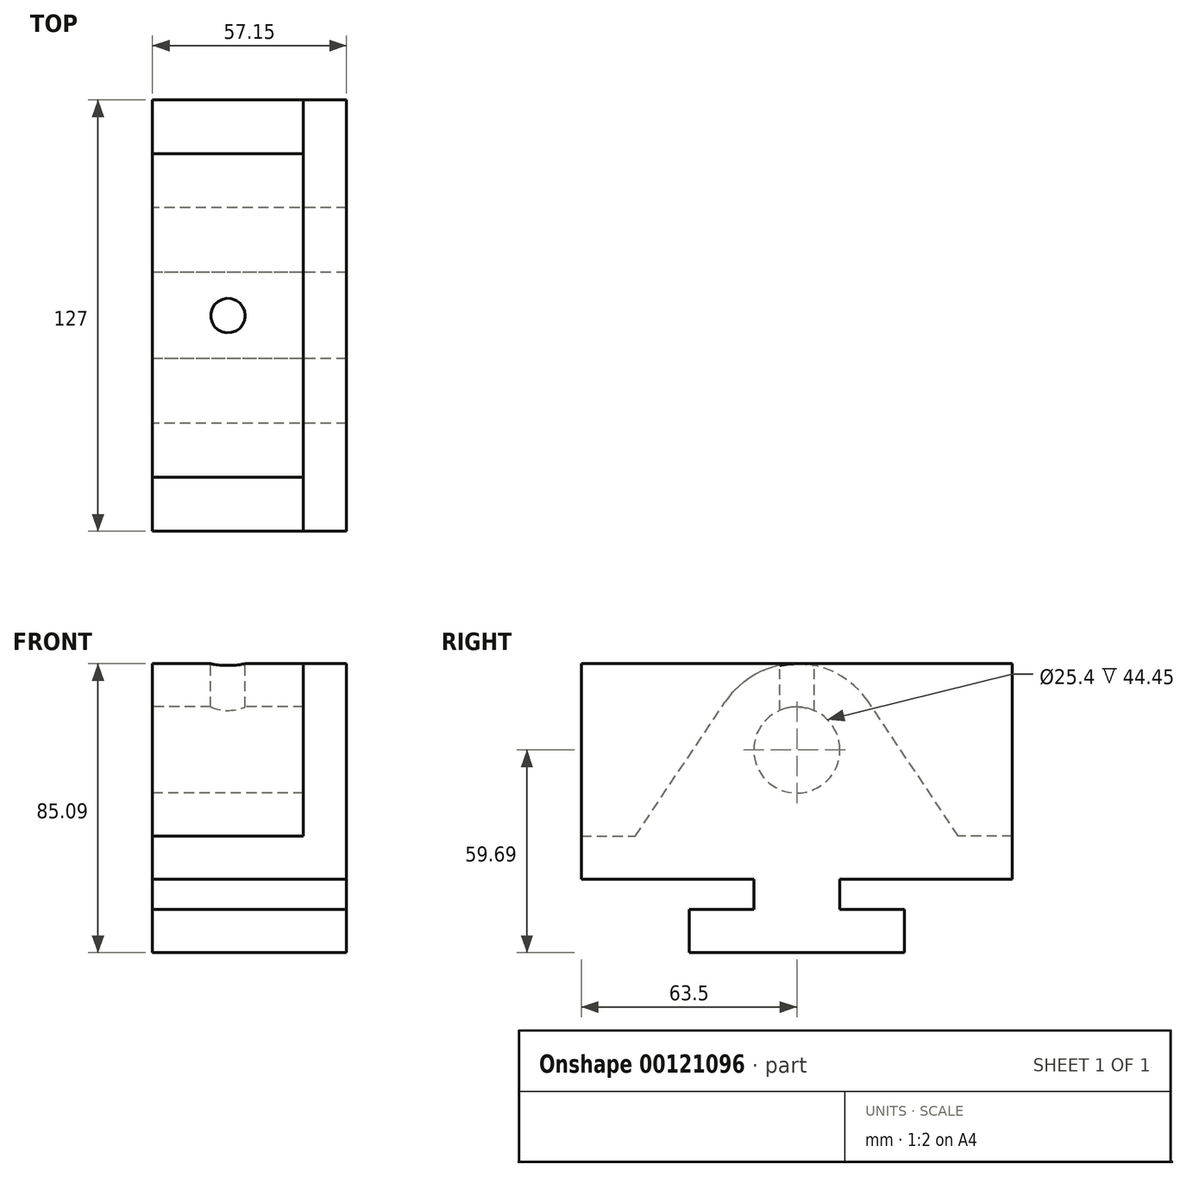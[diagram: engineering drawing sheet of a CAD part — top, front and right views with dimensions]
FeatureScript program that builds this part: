
annotation { "Feature Type Name" : "Feature", "Feature Type Description" : "" }
export const myFeature = defineFeature(function(context is Context, id is Id, definition is map)
    precondition{}
    {
        {
            var Q0;
            Q0=qCreatedBy(makeId("Right.planeOp"),FACE);
            var sketch = newSketch(context, id + "F0", { "sketchPlane" : qUnion([Q0])});
            skLineSegment(sketch, "E0", {"start": v(-31.75, 0) * mm, "end": v(31.75, 0) * mm});
            skLineSegment(sketch, "E1", {"start": v(31.75, 0) * mm, "end": v(31.75, 12.7) * mm});
            skLineSegment(sketch, "E2", {"start": v(31.75, 12.7) * mm, "end": v(12.7, 12.7) * mm});
            skLineSegment(sketch, "E3", {"start": v(12.7, 12.7) * mm, "end": v(12.7, 21.59) * mm});
            skLineSegment(sketch, "E4", {"start": v(12.7, 21.59) * mm, "end": v(63.5, 21.59) * mm});
            skLineSegment(sketch, "E5", {"start": v(63.5, 21.59) * mm, "end": v(63.5, 85.1) * mm});
            skLineSegment(sketch, "E6", {"start": v(63.5, 85.1) * mm, "end": v(-63.5, 85.1) * mm});
            skLineSegment(sketch, "E7", {"start": v(-63.5, 85.1) * mm, "end": v(-63.5, 21.59) * mm});
            skLineSegment(sketch, "E8", {"start": v(-63.5, 21.59) * mm, "end": v(-12.7, 21.6) * mm});
            skLineSegment(sketch, "E9", {"start": v(-12.7, 21.6) * mm, "end": v(-12.7, 12.7) * mm});
            skLineSegment(sketch, "E10", {"start": v(-12.7, 12.7) * mm, "end": v(-31.75, 12.7) * mm});
            skLineSegment(sketch, "E11", {"start": v(-31.75, 12.7) * mm, "end": v(-31.75, 0) * mm});
            skSolve(sketch);
        }
        {
            var Q0;
            Q0 = qSketchRegion(id + "F0", true);
            extrude(context, id + "F1", {"entities" : qUnion([Q0]), "depth" : 57.15 * mm});
        }
        {
            var Q0;
            Q0=makeQuery(id+"F1.opExtrude","CAP_FACE",FACE,{"disambiguationData":[OSD([sQuery(id+"F0.wireOp",EDGE,"E0"),sQuery(id+"F0.wireOp",EDGE,"E1"),sQuery(id+"F0.wireOp",EDGE,"E2"),sQuery(id+"F0.wireOp",EDGE,"E3"),sQuery(id+"F0.wireOp",EDGE,"E4"),sQuery(id+"F0.wireOp",EDGE,"E5"),sQuery(id+"F0.wireOp",EDGE,"E6"),sQuery(id+"F0.wireOp",EDGE,"E7"),sQuery(id+"F0.wireOp",EDGE,"E8"),sQuery(id+"F0.wireOp",EDGE,"E9"),sQuery(id+"F0.wireOp",EDGE,"E10"),sQuery(id+"F0.wireOp",EDGE,"E11")])],"isStart":true});
            var sketch = newSketch(context, id + "F2", { "sketchPlane" : qUnion([Q0])});
            skLineSegment(sketch, "E12", {"start": v(-63.5, 34.3) * mm, "end": v(-47.63, 34.3) * mm});
            skLineSegment(sketch, "E13", {"start": v(63.5, 34.3) * mm, "end": v(47.62, 34.3) * mm});
            skArc(sketch, "E14", {"start": v(21.1, 73.84) * mm, "mid": v(0, 85.1) * mm, "end": v(-21.1, 73.84) * mm});
            skLineSegment(sketch, "E15", {"start": v(-47.63, 34.3) * mm, "end": v(-21.1, 73.84) * mm});
            skLineSegment(sketch, "E16", {"start": v(47.62, 34.3) * mm, "end": v(21.1, 73.84) * mm});
            skCircle(sketch, "E17", {"center": v(0, 59.7) * mm, "radius": 12.7 * mm});
            skLineSegment(sketch, "E18", {"start": v(-63.5, 34.3) * mm, "end": v(-63.5, 85.1) * mm});
            skLineSegment(sketch, "E19", {"start": v(-63.5, 85.1) * mm, "end": v(63.5, 85.1) * mm});
            skLineSegment(sketch, "E20", {"start": v(63.5, 85.1) * mm, "end": v(63.5, 34.3) * mm});
            skSolve(sketch);
        }
        {
            var Q0;
            Q0 = qSketchRegion(id + "F2", true);
            extrude(context, id + "F3", {"entities" : qUnion([Q0]), "operationType" : NewBodyOperationType.REMOVE, "oppositeDirection" : true, "depth" : 44.45 * mm});
        }
        {
            var Q0;
            Q0=makeQuery(id+"F1.opExtrude","SWEPT_FACE",FACE,{"disambiguationData":[OSD([sQuery(id+"F0.wireOp",EDGE,"E6")])]});
            var sketch = newSketch(context, id + "F4", { "sketchPlane" : qUnion([Q0])});
            skCircle(sketch, "E21", {"center": v(22.23, 0) * mm, "radius": 5.08 * mm});
            skSolve(sketch);
        }
        {
            var Q0;
            Q0 = qSketchRegion(id + "F4", true);
            extrude(context, id + "F5", {"entities" : qUnion([Q0]), "operationType" : NewBodyOperationType.REMOVE, "oppositeDirection" : true, "depth" : 15.24 * mm});
        }
    });
